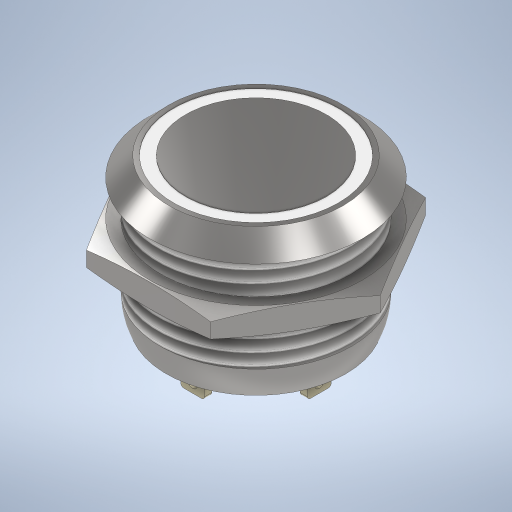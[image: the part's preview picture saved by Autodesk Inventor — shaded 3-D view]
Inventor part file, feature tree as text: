
AUTODESK INVENTOR PART (.ipt)
format: ipt  version: 2024 (Build 280153000, 153)  size: 458,752 bytes
history: native  units: mm
features: extrude x5, sketch x5, plane x2, chamfer x2, projected_geometry x2, revolve x1, fillet x1, pattern_circular x1, thread x1, other x1
ambient origin geometry x8: Origin, YZ Plane, XZ Plane, XY Plane, X Axis, Y Axis, Z Axis, Center Point
bodies: Solid1 (feature_tree)
feature tree (21):
  revolve  "Revolution1"  [1 undecoded]
  extrude  "Extrusion1"  Depth=8.9mm
  plane  "Work Plane1"
  extrude  "Extrusion2"  Depth=0.5mm
  fillet  "Fillet1"  Radius=2.0mm
  extrude  "Extrusion3"  Depth=11.8mm
  pattern_circular  "Circular Pattern1"  [2 undecoded]
  thread  "Thread1"  [1 undecoded]
  plane  "Work Plane2"
  sketch  "Sketch5"  dims[d10=1.0mm d11=0.05mm d12=0.0mm d13=10.5mm d14=13.0mm d15=2.0mm d16=0.6mm d17=5.0mm d18=0.05mm d19=0.0mm d20=0.25mm d21=0.8mm d22=0.75mm d23=0.5mm d24=10.0mm d25=0.0mm d26=40.0mm d27=360.0deg d29=10.0mm d30=0.0mm d31=3.0mm d32=21.8mm d33=18.0mm d34=2.0mm d35=0.0mm d36=0.5mm d37=2.0mm d38=45.0deg d39=0.5mm d40=2.0mm d41=45.0deg d42=0.0mm d43=0.0mm]
  extrude  "Extrusion4"  Depth=18.0mm
  chamfer  "Chamfer1"  Distance=2.0mm
  chamfer  "Chamfer2"  Distance=0.6mm
  extrude  "Extrusion5"  Depth=18.0mm
  sketch  "Sketch1"  dims[d0=8.0mm d1=1.6mm]
  sketch  "Sketch2"  dims[d2=135.0deg d3=8.9mm]
  sketch  "Sketch3"  dims[d5=0.25mm d6=0.5mm d7=2.0mm]
  sketch  "Sketch4"  dims[d8=90.0deg d9=11.8mm]
  projected_geometry  "Projected Loop1"
  other  "Nut"
  projected_geometry  "Project Cut Edges1"
note: 4 required parameter values undecoded (feature->parameter linkage not recoverable at this tier; creation-order binding heuristic only, values carry confidence <= 0.55)